# Revit family: Genelec_4420
name_source: partatom
category: Generic Models
units: mm (PartAtom-declared; Revit-internal decimal feet)

## family parameters
Always vertical = No
Can host rebar = No
Cut with Voids When Loaded = No
Maintain Annotation Orientation = No
Part Type = Normal
Room Calculation Point = Yes
Round Connector Dimension = Use Diameter
Shared = No
Work Plane-Based = No

## types (2) — shared parameters
Accuracy of Frequency Response = ± 1.5 dB (62 Hz - 20 kHz)
Acoustic Axis = 130
BIMobject category = Audio Electronics
Connections = 1 x RJ45 for PoE power, management and audio in AES67 / Dante format
1 x Euroblock Analog Input
Default Elevation = 1200 mm
Depth = 142 mm  [stored 0.465879 ft]
Description = The 4420A Smart IP Active PoE-Powered Installation Loudspeaker packs the power and flexibility of Smart IP technology into a compact enclosure, bringing clarity, intelligibility and uniform room coverage to all room geometries.
Dispersion Angle = H 120° V 100°
Driver Dimensions = ⌀ 105 mm Woofer + ⌀ 19 mm Tweeter
Export Type to IFC As = IfcAudioVisualApplianceType
Finish Type = Die cast aluminium
Frequency Response = 55 Hz - 39 kHz (-6 dB)
Height = 226 mm  [stored 0.74147 ft]
IFC Classification = Electric Appliance
IFC Name = 4420A
Line Drawing = https://assets.ctfassets.net
Mains Voltage = PoE+/PoE
Manufacturer = GENELEC
Manufacturer Country = Finland
Max. short term sine wave acoustic output  on axis in half space, averaged from 100Hz to 3 kHz = ≥ 100 dB SPL
Maximum long term RMS acoustic output in same conditions with IEC weighted noise (limited by driver unit protection circuit) = ≥ 93 dB SPL
Model = 4420
Model Description = Smart IP Installation Speaker
Model Image = https://images.ctfassets.net
Model Name = 4420A
Mounting Type = Includes mount: 4000-410B/W
Power Consumption = 26 W
Power consumption Idle = ≤5 W
Power consumption Standby = ≤4 W (ISS Active)
Price List Description = Recycled-aluminium cabinet with tightly controlled directivity and minimum diffraction for excellent clarity and intelligibility. Both drivers have metal protection grilles, with 105 mm (4 in) LF and 19 mm (3/4 in) HF transducers. Integrated crossover and Class D amplifiers 50 W + 50 W. Max. SPL 100 dB, frequency response 55 Hz - 39 kHz (-6 dB). Control by Smart IP Manager software, including device discovery, room equalisation, system organisation and status monitoring. On-Off switch on the rear panel. Dimensions: H 226 x W 151 x D 142 mm, weight 3.1 kg.
Product Family = Installation Speaker
Product Group = 4000 Series Installation Speakers
Self-generated Noise = ≤5 dB
Type IFC Predefined Type = SPEAKER
Type Image = <None>
URL = https://www.genelec.com
Uniclass 2.0 Description = Sound Amplifiers
Weight = 3.1
Width = 151 mm  [stored 0.495407 ft]

## per-type parameters (varying)
| type | Color | Horizontal Visibility | Vertical Visibility |
| 4420 Vertical | RAL_1002_Sand Yellow | No | Yes |
| 4420 Horizontal | RAL_8025_Pale Brown | Yes | No |

note: [stored X ft] marks values corroborated as IEEE doubles in the binary element streams (Revit-internal decimal feet)
